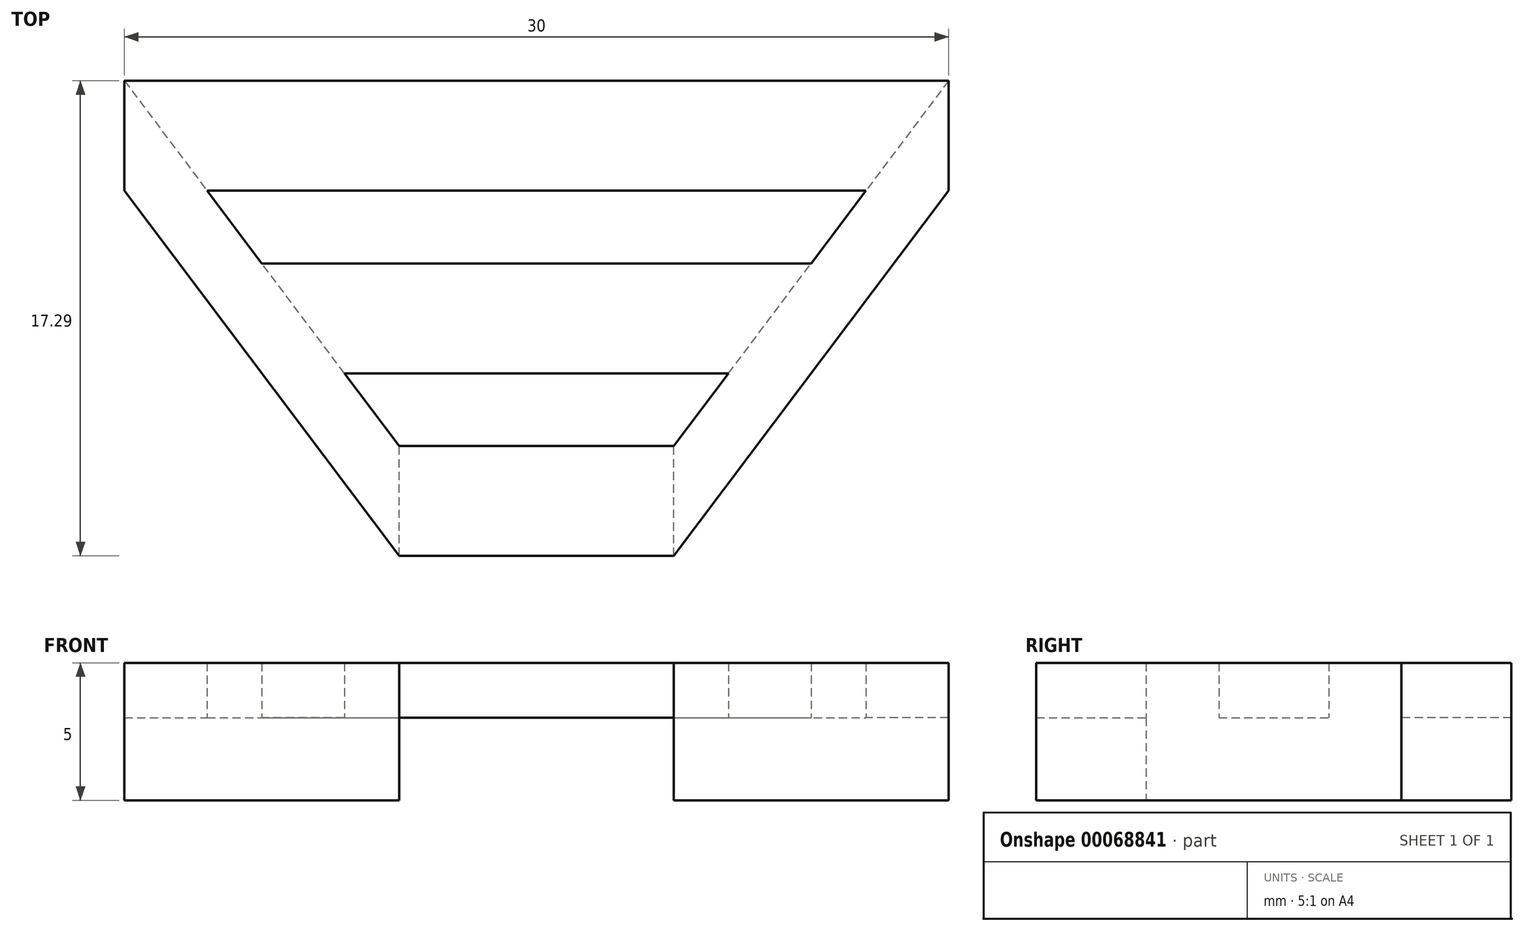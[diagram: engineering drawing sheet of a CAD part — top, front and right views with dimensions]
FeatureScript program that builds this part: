
annotation { "Feature Type Name" : "Feature", "Feature Type Description" : "" }
export const myFeature = defineFeature(function(context is Context, id is Id, definition is map)
    precondition{}
    {
        {
            var Q0;
            Q0=qCreatedBy(makeId("Top.planeOp"),FACE);
            var sketch = newSketch(context, id + "F0", { "sketchPlane" : qUnion([Q0])});
            skLineSegment(sketch, "E0.rect.bottom", {"start": v(-15, 17.94) * mm, "end": v(15, 17.94) * mm});
            skLineSegment(sketch, "E0.rect.top", {"start": v(-15, 21.94) * mm, "end": v(15, 21.94) * mm});
            skLineSegment(sketch, "E0.rect.left", {"start": v(-15, 17.94) * mm, "end": v(-15, 21.94) * mm});
            skLineSegment(sketch, "E0.rect.right", {"start": v(15, 17.94) * mm, "end": v(15, 21.94) * mm});
            skPoint(sketch, "E0.rect.middle", {"position": v(0, 19.94) * mm});
            skLineSegment(sketch, "E1.rect.bottom", {"start": v(-10, 11.3) * mm, "end": v(10, 11.3) * mm});
            skLineSegment(sketch, "E1.rect.top", {"start": v(-10, 15.3) * mm, "end": v(10, 15.3) * mm});
            skLineSegment(sketch, "E1.rect.left", {"start": v(-10, 11.3) * mm, "end": v(-10, 15.3) * mm});
            skLineSegment(sketch, "E1.rect.right", {"start": v(10, 11.3) * mm, "end": v(10, 15.3) * mm});
            skPoint(sketch, "E1.rect.middle", {"position": v(0, 13.3) * mm});
            skLineSegment(sketch, "E2.rect.bottom", {"start": v(-5, 4.65) * mm, "end": v(5, 4.65) * mm});
            skLineSegment(sketch, "E2.rect.top", {"start": v(-5, 8.65) * mm, "end": v(5, 8.65) * mm});
            skLineSegment(sketch, "E2.rect.left", {"start": v(-5, 4.65) * mm, "end": v(-5, 8.65) * mm});
            skLineSegment(sketch, "E2.rect.right", {"start": v(5, 4.65) * mm, "end": v(5, 8.65) * mm});
            skPoint(sketch, "E2.rect.middle", {"position": v(0, 6.65) * mm});
            skLineSegment(sketch, "E3", {"start": v(0, 19.94) * mm, "end": v(0, 13.3) * mm, "construction": true});
            skLineSegment(sketch, "E4", {"start": v(0, 6.65) * mm, "end": v(0, 13.3) * mm, "construction": true});
            skLineSegment(sketch, "E5", {"start": v(0, 6.65) * mm, "end": v(0, 0) * mm, "construction": true});
            skLineSegment(sketch, "E6", {"start": v(-15, 17.94) * mm, "end": v(-10, 11.3) * mm});
            skLineSegment(sketch, "E7", {"start": v(-5, 4.65) * mm, "end": v(-10, 11.3) * mm});
            skLineSegment(sketch, "E8", {"start": v(-15, 21.94) * mm, "end": v(-10, 15.3) * mm});
            skLineSegment(sketch, "E9", {"start": v(-5, 8.65) * mm, "end": v(-10, 15.3) * mm});
            skLineSegment(sketch, "E10", {"start": v(10, 11.3) * mm, "end": v(15, 17.94) * mm});
            skLineSegment(sketch, "E11", {"start": v(15, 21.94) * mm, "end": v(10, 15.3) * mm});
            skLineSegment(sketch, "E12", {"start": v(5, 8.65) * mm, "end": v(10, 15.3) * mm});
            skLineSegment(sketch, "E13", {"start": v(10, 11.3) * mm, "end": v(5, 4.65) * mm});
            skSolve(sketch);
        }
        {
            var Q0;
            {var subQ0=sQuery(id+"F0.wireOp",EDGE,"E0.rect.left");Q0=makeQuery(id+"F0.imprint","IMPRINT",FACE,{"disambiguationData":[TD([[makeQuery(id+"F0.imprint","IMPRINT",EDGE,{"derivedFrom":subQ0}),-1.0]])]});}
            var Q1;
            {var subQ4=sQuery(id+"F0.wireOp",EDGE,"E1.rect.left");Q1=makeQuery(id+"F0.imprint","IMPRINT",FACE,{"disambiguationData":[TD([[makeQuery(id+"F0.imprint","IMPRINT",EDGE,{"derivedFrom":subQ4}),1.0]])]});}
            var Q2;
            {var subQ0=sQuery(id+"F0.wireOp",EDGE,"E1.rect.left");Q2=makeQuery(id+"F0.imprint","IMPRINT",FACE,{"disambiguationData":[TD([[makeQuery(id+"F0.imprint","IMPRINT",EDGE,{"derivedFrom":subQ0}),-1.0]])]});}
            var Q3;
            {var subQ4=sQuery(id+"F0.wireOp",EDGE,"E2.rect.left");Q3=makeQuery(id+"F0.imprint","IMPRINT",FACE,{"disambiguationData":[TD([[makeQuery(id+"F0.imprint","IMPRINT",EDGE,{"derivedFrom":subQ4}),1.0]])]});}
            var Q4;
            {var subQ4=sQuery(id+"F0.wireOp",EDGE,"E2.rect.right");Q4=makeQuery(id+"F0.imprint","IMPRINT",FACE,{"disambiguationData":[TD([[makeQuery(id+"F0.imprint","IMPRINT",EDGE,{"derivedFrom":subQ4}),-1.0]])]});}
            var Q5;
            {var subQ0=sQuery(id+"F0.wireOp",EDGE,"E1.rect.right");Q5=makeQuery(id+"F0.imprint","IMPRINT",FACE,{"disambiguationData":[TD([[makeQuery(id+"F0.imprint","IMPRINT",EDGE,{"derivedFrom":subQ0}),1.0]])]});}
            var Q6;
            {var subQ4=sQuery(id+"F0.wireOp",EDGE,"E1.rect.right");Q6=makeQuery(id+"F0.imprint","IMPRINT",FACE,{"disambiguationData":[TD([[makeQuery(id+"F0.imprint","IMPRINT",EDGE,{"derivedFrom":subQ4}),-1.0]])]});}
            var Q7;
            {var subQ0=sQuery(id+"F0.wireOp",EDGE,"E0.rect.right");Q7=makeQuery(id+"F0.imprint","IMPRINT",FACE,{"disambiguationData":[TD([[makeQuery(id+"F0.imprint","IMPRINT",EDGE,{"derivedFrom":subQ0}),1.0]])]});}
            extrude(context, id + "F1", {"entities" : qUnion([Q0, Q1, Q2, Q3, Q4, Q5, Q6, Q7]), "depth" : 5 * mm});
        }
        {
            var Q0;
            Q0=makeQuery(id+"F0.imprint","IMPRINT",FACE,{"disambiguationData":[TD([[makeQuery(id+"F0.imprint","IMPRINT",EDGE,{"derivedFrom":sQuery(id+"F0.wireOp",EDGE,"E2.rect.bottom")}),1.0]])]});
            var Q1;
            {var subQ5=sQuery(id+"F0.wireOp",EDGE,"E1.rect.top");Q1=makeQuery(id+"F0.imprint","IMPRINT",FACE,{"disambiguationData":[TD([[makeQuery(id+"F0.imprint","IMPRINT",EDGE,{"derivedFrom":subQ5}),-1.0]])]});}
            var Q2;
            {var subQ5=sQuery(id+"F0.wireOp",EDGE,"E0.rect.top");Q2=makeQuery(id+"F0.imprint","IMPRINT",FACE,{"disambiguationData":[TD([[makeQuery(id+"F0.imprint","IMPRINT",EDGE,{"derivedFrom":subQ5}),-1.0]])]});}
            extrude(context, id + "F2", {"entities" : qUnion([Q0, Q1, Q2]), "operationType" : NewBodyOperationType.ADD, "depth" : 5 * mm, "hasSecondDirection" : true, "secondDirectionOppositeDirection" : false, "secondDirectionDepth" : 3 * mm});
        }
    });
